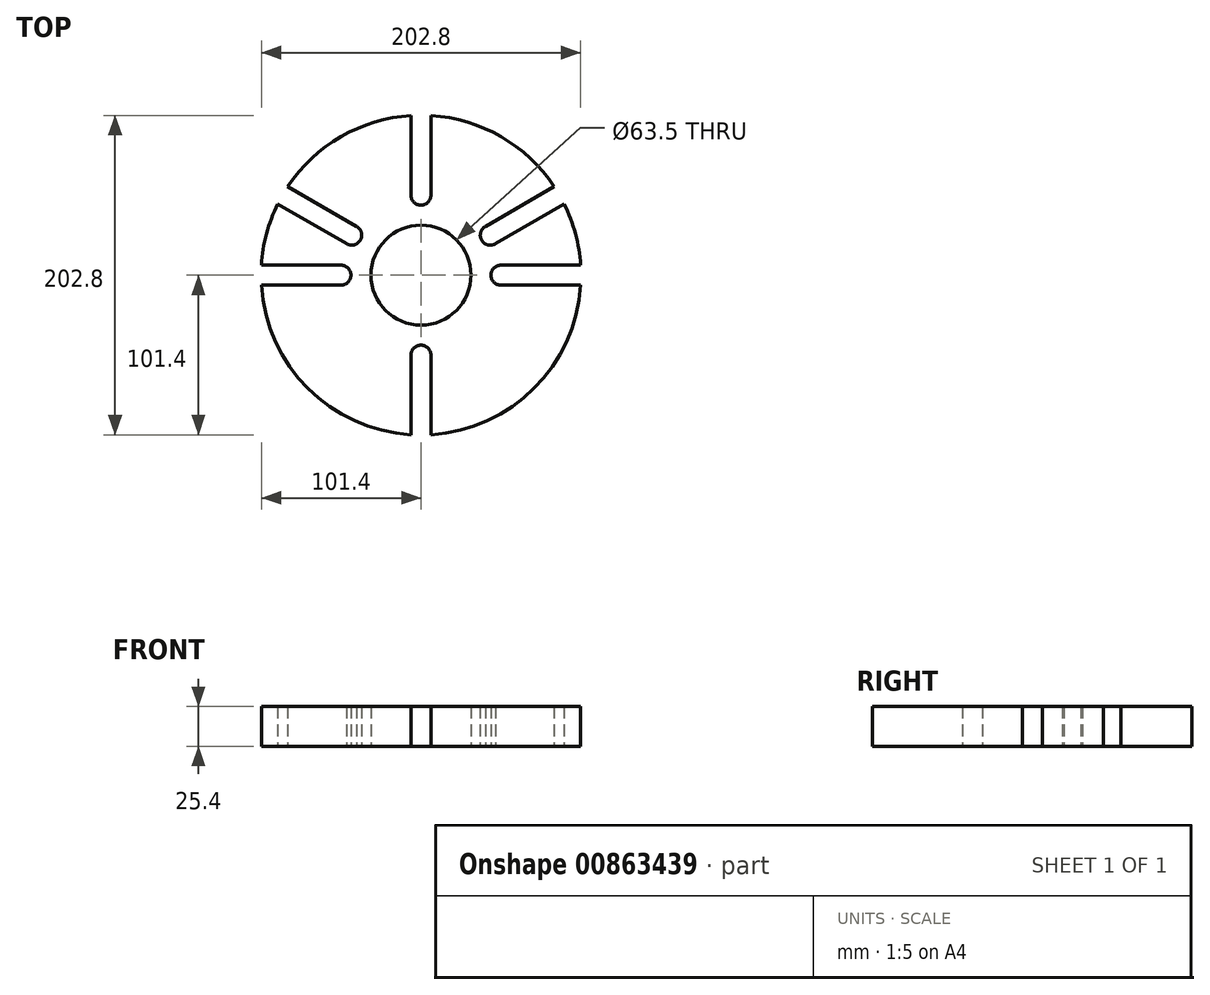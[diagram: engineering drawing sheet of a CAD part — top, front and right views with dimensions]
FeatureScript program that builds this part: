
annotation { "Feature Type Name" : "Feature", "Feature Type Description" : "" }
export const myFeature = defineFeature(function(context is Context, id is Id, definition is map)
    precondition{}
    {
        {
            var Q0;
            Q0=qCreatedBy(makeId("Top.planeOp"),FACE);
            var sketch = newSketch(context, id + "F0", { "sketchPlane" : qUnion([Q0])});
            skCircle(sketch, "E0", {"center": v(0, 0) * mm, "radius": 101.6 * mm});
            skCircle(sketch, "E1", {"center": v(-50.8, 0) * mm, "radius": 6.35 * mm});
            skCircle(sketch, "E2", {"center": v(0, 50.8) * mm, "radius": 6.35 * mm});
            skCircle(sketch, "E3", {"center": v(50.8, 0) * mm, "radius": 6.35 * mm});
            skCircle(sketch, "E4", {"center": v(0, -50.8) * mm, "radius": 6.35 * mm});
            skLineSegment(sketch, "E5", {"start": v(0, 0) * mm, "end": v(-58.2, 33.6) * mm, "construction": true});
            skLineSegment(sketch, "E6", {"start": v(0, 0) * mm, "end": v(87.99, 50.8) * mm, "construction": true});
            skLineSegment(sketch, "E7", {"start": v(0, 0) * mm, "end": v(0, -29.06) * mm, "construction": true});
            skCircle(sketch, "E8", {"center": v(-44, 25.4) * mm, "radius": 6.35 * mm});
            skCircle(sketch, "E9", {"center": v(44, 25.4) * mm, "radius": 6.35 * mm});
            skLineSegment(sketch, "E10", {"start": v(-50.8, -6.35) * mm, "end": v(-101.4, -6.35) * mm});
            skLineSegment(sketch, "E11", {"start": v(-50.8, 6.35) * mm, "end": v(-101.4, 6.35) * mm});
            skLineSegment(sketch, "E12.1.0", {"start": v(-6.35, -50.8) * mm, "end": v(-6.35, -101.4) * mm});
            skLineSegment(sketch, "E12.1.1", {"start": v(6.35, -50.8) * mm, "end": v(6.35, -101.4) * mm});
            skLineSegment(sketch, "E12.2.0", {"start": v(50.8, -6.35) * mm, "end": v(101.4, -6.35) * mm});
            skLineSegment(sketch, "E12.2.1", {"start": v(50.8, 6.35) * mm, "end": v(101.4, 6.35) * mm});
            skLineSegment(sketch, "E12.3.0", {"start": v(6.35, 50.8) * mm, "end": v(6.35, 101.4) * mm});
            skLineSegment(sketch, "E12.3.1", {"start": v(-6.35, 50.8) * mm, "end": v(-6.35, 101.4) * mm});
            skLineSegment(sketch, "E13", {"start": v(-44, 25.4) * mm, "end": v(-47.07, 19.84) * mm});
            skLineSegment(sketch, "E14", {"start": v(-47.07, 19.84) * mm, "end": v(-91, 45.2) * mm});
            skLineSegment(sketch, "E15", {"start": v(-44, 25.4) * mm, "end": v(-40.92, 30.96) * mm});
            skLineSegment(sketch, "E16", {"start": v(-40.92, 30.96) * mm, "end": v(-84.64, 56.2) * mm});
            skLineSegment(sketch, "E17.1.0", {"start": v(40.72, 30.84) * mm, "end": v(84.64, 56.2) * mm});
            skLineSegment(sketch, "E17.1.1", {"start": v(47.27, 19.96) * mm, "end": v(91, 45.2) * mm});
            skLineSegment(sketch, "E17.anchor1", {"start": v(0, 0) * mm, "end": v(-91, 45.2) * mm, "construction": true});
            skLineSegment(sketch, "E17.anchor2", {"start": v(0, 0) * mm, "end": v(84.64, 56.2) * mm, "construction": true});
            skCircle(sketch, "E18", {"center": v(0, 0) * mm, "radius": 31.75 * mm});
            skSolve(sketch);
        }
        {
            var Q0;
            {var subQ3=sQuery(id+"F0.wireOp",EDGE,"E10");Q0=makeQuery(id+"F0.imprint","IMPRINT",FACE,{"disambiguationData":[TD([[makeQuery(id+"F0.imprint","IMPRINT",EDGE,{"derivedFrom":subQ3}),1.0]])]});}
            extrude(context, id + "F1", {"entities" : qUnion([Q0]), "depth" : 25.4 * mm, "offsetDistance" : 25.4 * mm});
        }
    });
